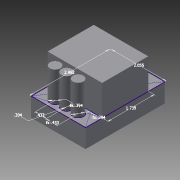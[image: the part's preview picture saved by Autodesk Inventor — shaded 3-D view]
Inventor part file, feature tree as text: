
AUTODESK INVENTOR PART (.ipt)
format: ipt  version: 2015 SP1 (Build 190203100, 203)  size: 94,208 bytes
history: native  units: in
note: dims shown in document units (in); Inventor stores cm internally (conversion verified against a paired STEP export)
features: extrude x3, sketch x1
ambient origin geometry x8: Origin, YZ Plane, XZ Plane, XY Plane, X Axis, Y Axis, Z Axis, Center Point
bodies: Solid1 (feature_tree)
feature tree (4):
  sketch  "Sketch2"  dims[d0=2.0551in d1=2.9921in d2=1.739in d4=0.7087in d5=0.0in d6=1.1417in d7=0.0in d9=0.3937in d10=0.3937in d11=0.4331in d12=0.4331in d13=1.1417in d14=0.0in]
  extrude  "Extrusion1"  Depth=2.9921in
  extrude  "Extrusion2"  Depth=1.739in
  extrude  "Extrusion3"  Depth=0.7087in TaperAngle=0.0deg
